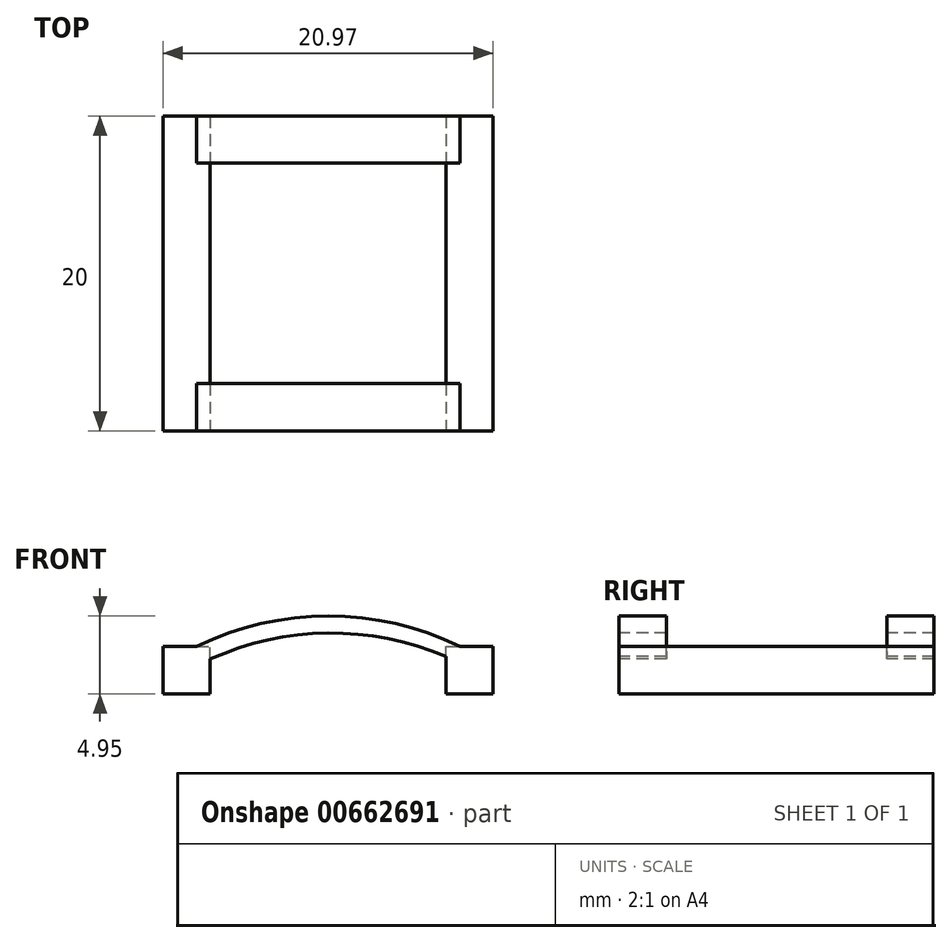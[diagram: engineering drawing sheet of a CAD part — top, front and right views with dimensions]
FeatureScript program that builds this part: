
annotation { "Feature Type Name" : "Feature", "Feature Type Description" : "" }
export const myFeature = defineFeature(function(context is Context, id is Id, definition is map)
    precondition{}
    {
        {
            var Q0;
            Q0=qCreatedBy(makeId("Top.planeOp"),FACE);
            var sketch = newSketch(context, id + "F0", { "sketchPlane" : qUnion([Q0])});
            skLineSegment(sketch, "E0.bottom", {"start": v(0, 0) * mm, "end": v(3, 0) * mm});
            skLineSegment(sketch, "E0.top", {"start": v(0, 20) * mm, "end": v(3, 20) * mm});
            skLineSegment(sketch, "E0.left", {"start": v(0, 0) * mm, "end": v(0, 20) * mm});
            skLineSegment(sketch, "E0.right", {"start": v(3, 0) * mm, "end": v(3, 20) * mm});
            skLineSegment(sketch, "E1.bottom", {"start": v(17.97, 0) * mm, "end": v(20.97, 0) * mm});
            skLineSegment(sketch, "E1.top", {"start": v(17.97, 20) * mm, "end": v(20.97, 20) * mm});
            skLineSegment(sketch, "E1.left", {"start": v(17.97, 0) * mm, "end": v(17.97, 20) * mm});
            skLineSegment(sketch, "E1.right", {"start": v(20.97, 0) * mm, "end": v(20.97, 20) * mm});
            skSolve(sketch);
        }
        {
            var Q0;
            Q0=qSketchRegion(id+"F0",true);
            extrude(context, id + "F1", {"entities" : qUnion([Q0]), "depth" : 3 * mm, "offsetDistance" : 25 * mm});
        }
        {
            var Q0;
            Q0=qCreatedBy(makeId("Front.planeOp"),FACE);
            var sketch = newSketch(context, id + "F2", { "sketchPlane" : qUnion([Q0])});
            skArc(sketch, "E2", {"start": v(18, 2.37) * mm, "mid": v(10.47, 3.86) * mm, "end": v(2.98, 2.2) * mm});
            skArc(sketch, "E3", {"start": v(18.89, 2.98) * mm, "mid": v(10.49, 4.95) * mm, "end": v(2.09, 2.97) * mm});
            skLineSegment(sketch, "E4", {"start": v(2.09, 2.97) * mm, "end": v(2.98, 2.2) * mm});
            skLineSegment(sketch, "E5", {"start": v(18.89, 2.98) * mm, "end": v(18, 2.37) * mm});
            skSolve(sketch);
        }
        {
            var Q0;
            Q0=qSketchRegion(id+"F2",true);
            extrude(context, id + "F3", {"entities" : qUnion([Q0]), "operationType" : NewBodyOperationType.ADD, "oppositeDirection" : true, "depth" : 3 * mm, "offsetDistance" : 25 * mm});
        }
        {
            var Q0;
            Q0=makeQuery(id+"F2.imprint","IMPRINT",FACE,{"disambiguationData":[TD([[makeQuery(id+"F2.imprint","IMPRINT",EDGE,{"derivedFrom":sQuery(id+"F2.wireOp",EDGE,"E2")}),-1.0]])]});
            extrude(context, id + "F4", {"entities" : qUnion([Q0]), "operationType" : NewBodyOperationType.ADD, "oppositeDirection" : true, "depth" : 20 * mm, "offsetDistance" : 25 * mm, "hasSecondDirection" : true, "secondDirectionOppositeDirection" : true, "secondDirectionDepth" : 17 * mm});
        }
    });
